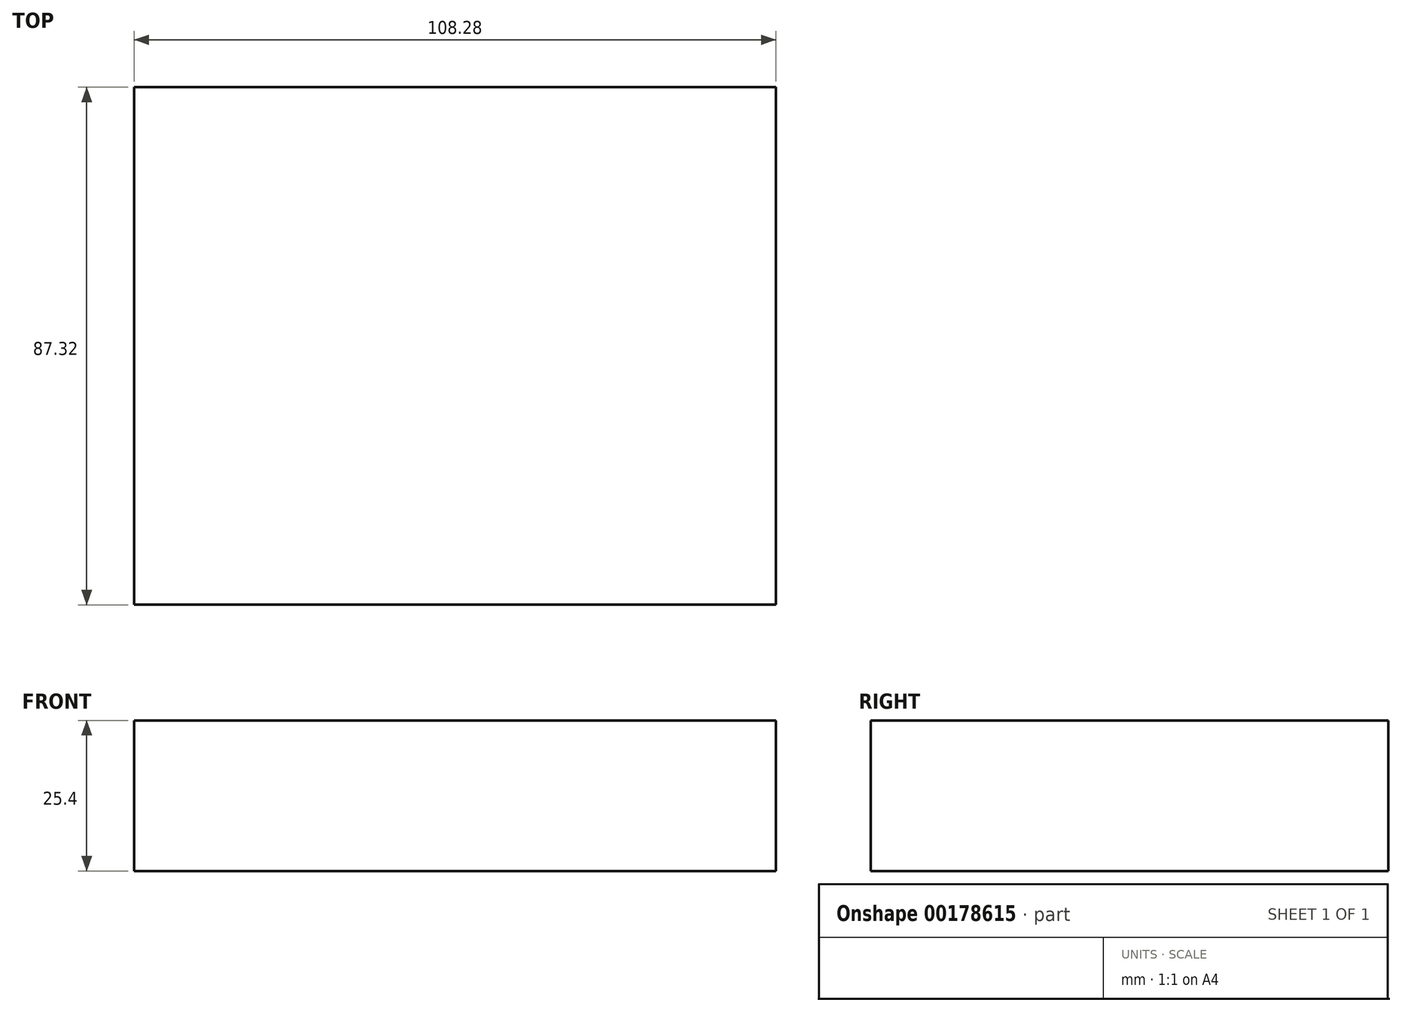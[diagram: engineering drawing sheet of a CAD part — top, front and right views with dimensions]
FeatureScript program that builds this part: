
annotation { "Feature Type Name" : "Feature", "Feature Type Description" : "" }
export const myFeature = defineFeature(function(context is Context, id is Id, definition is map)
    precondition{}
    {
        {
            var Q0;
            Q0=qCreatedBy(makeId("Top.planeOp"),FACE);
            var sketch = newSketch(context, id + "F0", { "sketchPlane" : qUnion([Q0])});
            skLineSegment(sketch, "E0.bottom", {"start": v(54.04, -30.93) * mm, "end": v(-54.24, -30.93) * mm});
            skLineSegment(sketch, "E0.top", {"start": v(54.04, 56.39) * mm, "end": v(-54.24, 56.39) * mm});
            skLineSegment(sketch, "E0.left", {"start": v(54.04, -30.93) * mm, "end": v(54.04, 56.39) * mm});
            skLineSegment(sketch, "E0.right", {"start": v(-54.24, -30.93) * mm, "end": v(-54.24, 56.39) * mm});
            skSolve(sketch);
        }
        {
            var Q0;
            Q0=makeQuery(id+"F0.imprint","IMPRINT",FACE,{"disambiguationData":[TD([[makeQuery(id+"F0.imprint","IMPRINT",EDGE,{"derivedFrom":sQuery(id+"F0.wireOp",EDGE,"E0.bottom")}),-1.0]])]});
            extrude(context, id + "F1", {"entities" : qUnion([Q0]), "depth" : 25.4 * mm, "offsetDistance" : 25.4 * mm});
        }
    });
